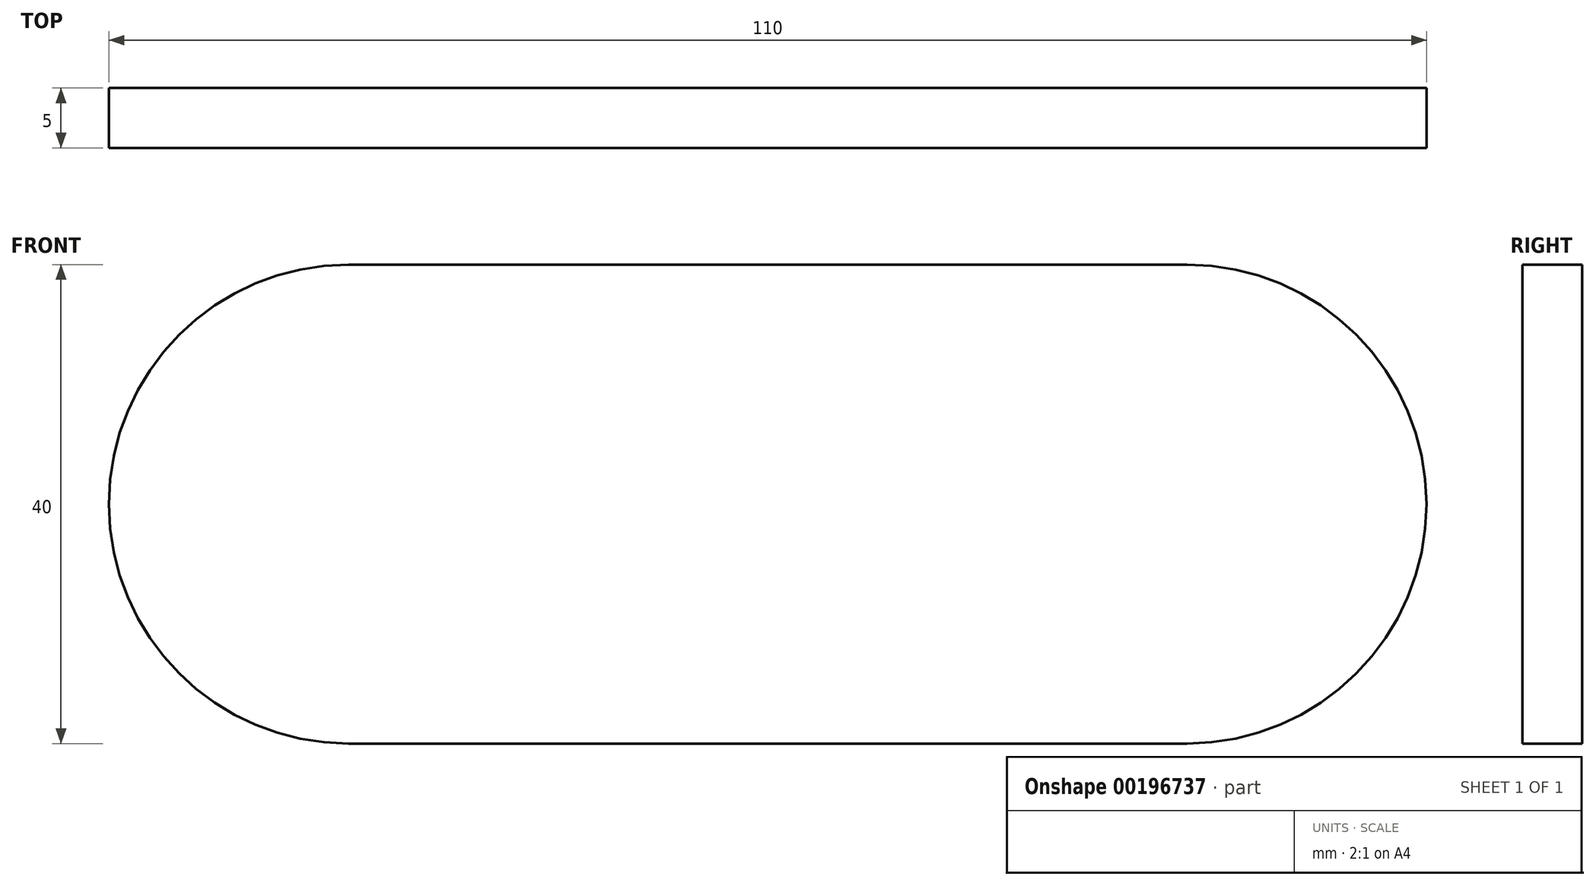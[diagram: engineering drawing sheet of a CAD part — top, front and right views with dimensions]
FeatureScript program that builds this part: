
annotation { "Feature Type Name" : "Feature", "Feature Type Description" : "" }
export const myFeature = defineFeature(function(context is Context, id is Id, definition is map)
    precondition{}
    {
        {
            var Q0;
            Q0=qCreatedBy(makeId("Front.planeOp"),FACE);
            var sketch = newSketch(context, id + "F0", { "sketchPlane" : qUnion([Q0])});
            skLineSegment(sketch, "E0.bottom", {"start": v(35, 20) * mm, "end": v(-35, 20) * mm});
            skLineSegment(sketch, "E0.top", {"start": v(35, -20) * mm, "end": v(-35, -20) * mm});
            skLineSegment(sketch, "E0.left", {"start": v(55, 0) * mm, "end": v(55, 0) * mm});
            skLineSegment(sketch, "E0.right", {"start": v(-55, 0) * mm, "end": v(-55, 0) * mm});
            skPoint(sketch, "E0.middle", {"position": v(0, 0) * mm});
            skPoint(sketch, "E1.visualSharp", {"position": v(-55, 20) * mm});
            skArc(sketch, "E1.filletArc", {"start": v(-35, 20) * mm, "mid": v(-49.14, 14.14) * mm, "end": v(-55, 0) * mm});
            skPoint(sketch, "E2.visualSharp", {"position": v(-55, -20) * mm});
            skArc(sketch, "E2.filletArc", {"start": v(-55, 0) * mm, "mid": v(-49.14, -14.14) * mm, "end": v(-35, -20) * mm});
            skPoint(sketch, "E3.visualSharp", {"position": v(55, 20) * mm});
            skArc(sketch, "E3.filletArc", {"start": v(55, 0) * mm, "mid": v(49.14, 14.14) * mm, "end": v(35, 20) * mm});
            skPoint(sketch, "E4.visualSharp", {"position": v(55, -20) * mm});
            skArc(sketch, "E4.filletArc", {"start": v(35, -20) * mm, "mid": v(49.14, -14.14) * mm, "end": v(55, 0) * mm});
            skCircle(sketch, "E5", {"center": v(35, 0) * mm, "radius": 12.5 * mm});
            skSolve(sketch);
        }
        {
            var Q0;
            Q0=makeQuery(id+"F0.imprint","IMPRINT",FACE,{"disambiguationData":[TD([[makeQuery(id+"F0.imprint","IMPRINT",EDGE,{"derivedFrom":sQuery(id+"F0.wireOp",EDGE,"E0.bottom")}),1.0]])]});
            var Q1;
            Q1=makeQuery(id+"F0.imprint","IMPRINT",FACE,{"disambiguationData":[TD([[makeQuery(id+"F0.imprint","IMPRINT",EDGE,{"derivedFrom":sQuery(id+"F0.wireOp",EDGE,"E5")}),1.0]])]});
            extrude(context, id + "F1", {"entities" : qUnion([Q0, Q1]), "endBound" : BoundingType.SYMMETRIC, "depth" : 5 * mm});
        }
    });
